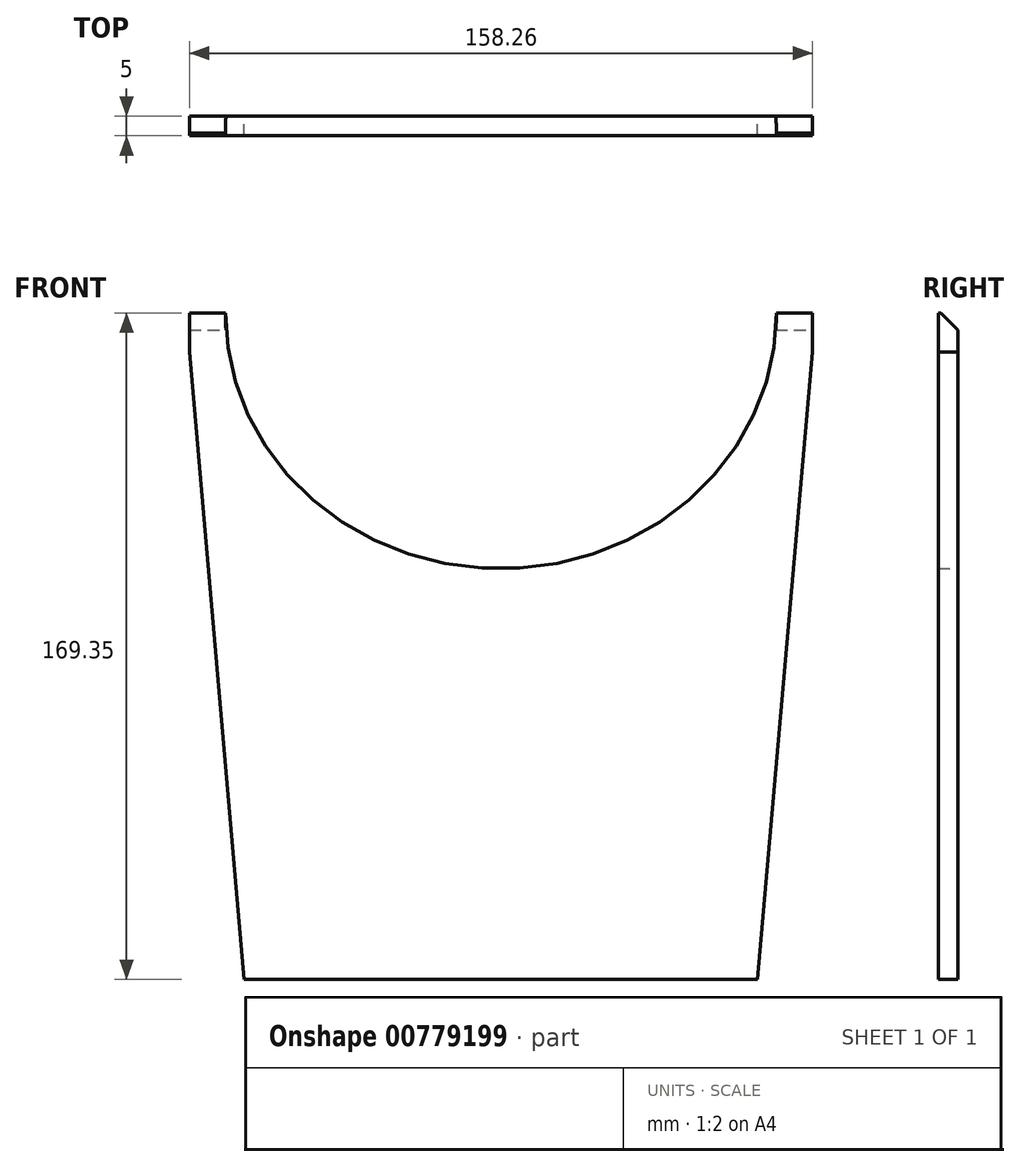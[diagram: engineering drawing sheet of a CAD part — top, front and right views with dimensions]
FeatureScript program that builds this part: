
annotation { "Feature Type Name" : "Feature", "Feature Type Description" : "" }
export const myFeature = defineFeature(function(context is Context, id is Id, definition is map)
    precondition{}
    {
        {
            var Q0;
            Q0=qCreatedBy(makeId("Front.planeOp"),FACE);
            var sketch = newSketch(context, id + "F0", { "sketchPlane" : qUnion([Q0])});
            skLineSegment(sketch, "E0", {"start": v(0, 0) * mm, "end": v(160, 0) * mm});
            skLineSegment(sketch, "E1", {"start": v(160, 0) * mm, "end": v(145.18, -169.35) * mm});
            skLineSegment(sketch, "E2", {"start": v(0, 0) * mm, "end": v(14.82, -169.35) * mm});
            skLineSegment(sketch, "E3", {"start": v(14.82, -169.35) * mm, "end": v(145.18, -169.35) * mm});
            skSolve(sketch);
        }
        {
            var Q0;
            Q0=qSketchRegion(id+"F0",true);
            extrude(context, id + "F1", {"entities" : qUnion([Q0]), "depth" : 5 * mm});
        }
        {
            var Q0;
            Q0=makeQuery(id+"F1.opExtrude","CAP_FACE",FACE,{"disambiguationData":[OSD([sQuery(id+"F0.wireOp",EDGE,"E0"),sQuery(id+"F0.wireOp",EDGE,"E1"),sQuery(id+"F0.wireOp",EDGE,"E2"),sQuery(id+"F0.wireOp",EDGE,"E3")])],"isStart":false});
            var sketch = newSketch(context, id + "F2", { "sketchPlane" : qUnion([Q0])});
            skEllipse(sketch, "E4", {"center": v(80, 0) * mm, "majorRadius": 65 * mm, "minorRadius": 70 * mm, "majorAxis": v(0, -1)});
            skSolve(sketch);
        }
        {
            var Q0;
            Q0=qSketchRegion(id+"F2",true);
            extrude(context, id + "F3", {"entities" : qUnion([Q0]), "operationType" : NewBodyOperationType.REMOVE, "oppositeDirection" : true, "depth" : 5 * mm});
        }
        {
            var Q0;
            Q0=makeQuery(id+"F1.opExtrude","CAP_FACE",FACE,{"disambiguationData":[OSD([sQuery(id+"F0.wireOp",EDGE,"E0"),sQuery(id+"F0.wireOp",EDGE,"E1"),sQuery(id+"F0.wireOp",EDGE,"E2"),sQuery(id+"F0.wireOp",EDGE,"E3")])],"isStart":true});
            var sketch = newSketch(context, id + "F4", { "sketchPlane" : qUnion([Q0])});
            skLineSegment(sketch, "E5.bottom", {"start": v(-160, 0) * mm, "end": v(-159.13, 0) * mm});
            skLineSegment(sketch, "E5.top", {"start": v(-160, -10) * mm, "end": v(-159.13, -10) * mm});
            skLineSegment(sketch, "E5.left", {"start": v(-160, 0) * mm, "end": v(-160, -10) * mm});
            skLineSegment(sketch, "E5.right", {"start": v(-159.13, 0) * mm, "end": v(-159.13, -10) * mm});
            skSolve(sketch);
        }
        {
            var Q0;
            Q0=qSketchRegion(id+"F4",true);
            extrude(context, id + "F5", {"entities" : qUnion([Q0]), "operationType" : NewBodyOperationType.REMOVE, "oppositeDirection" : true, "depth" : 5 * mm});
        }
        {
            var Q0;
            Q0=makeQuery(id+"F1.opExtrude","CAP_FACE",FACE,{"disambiguationData":[OSD([sQuery(id+"F0.wireOp",EDGE,"E0"),sQuery(id+"F0.wireOp",EDGE,"E1"),sQuery(id+"F0.wireOp",EDGE,"E2"),sQuery(id+"F0.wireOp",EDGE,"E3")])],"isStart":true});
            var sketch = newSketch(context, id + "F6", { "sketchPlane" : qUnion([Q0])});
            skLineSegment(sketch, "E6.bottom", {"start": v(0, 0) * mm, "end": v(-0.87, 0) * mm});
            skLineSegment(sketch, "E6.top", {"start": v(0, -10) * mm, "end": v(-0.87, -10) * mm});
            skLineSegment(sketch, "E6.left", {"start": v(0, 0) * mm, "end": v(0, -10) * mm});
            skLineSegment(sketch, "E6.right", {"start": v(-0.87, 0) * mm, "end": v(-0.87, -10) * mm});
            skSolve(sketch);
        }
        {
            var Q0;
            Q0=qSketchRegion(id+"F6",true);
            extrude(context, id + "F7", {"entities" : qUnion([Q0]), "operationType" : NewBodyOperationType.REMOVE, "oppositeDirection" : true, "depth" : 5 * mm});
        }
        {
            var Q0;
            Q0=makeQuery(id+"F5.boolean.opBoolean","COPY",FACE,{"derivedFrom":makeQuery(id+"F5.opExtrude","SWEPT_FACE",FACE,{"disambiguationData":[OSD([sQuery(id+"F4.wireOp",EDGE,"E5.right")])]})});
            var sketch = newSketch(context, id + "F8", { "sketchPlane" : qUnion([Q0])});
            skLineSegment(sketch, "E7", {"start": v(-4.38, 0) * mm, "end": v(0, -4.38) * mm});
            skLineSegment(sketch, "E8", {"start": v(0, -4.38) * mm, "end": v(0, 0) * mm});
            skLineSegment(sketch, "E9", {"start": v(0, 0) * mm, "end": v(-4.38, 0) * mm});
            skSolve(sketch);
        }
        {
            var Q0;
            Q0=qSketchRegion(id+"F8",true);
            extrude(context, id + "F9", {"entities" : qUnion([Q0]), "operationType" : NewBodyOperationType.REMOVE, "oppositeDirection" : true, "depth" : 160 * mm});
        }
    });
